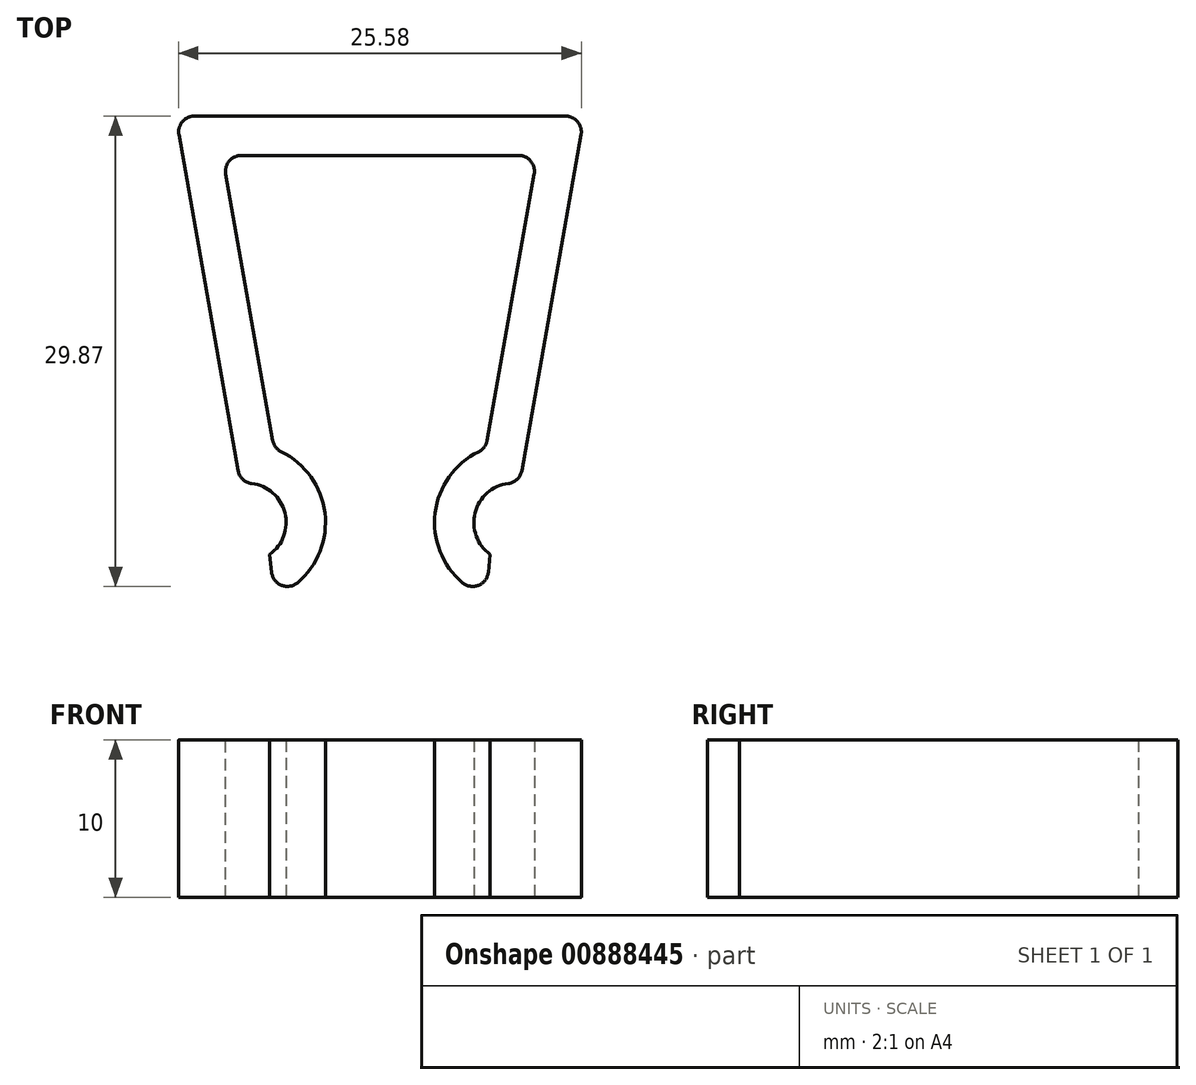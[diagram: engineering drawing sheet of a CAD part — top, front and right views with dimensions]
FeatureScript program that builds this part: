
annotation { "Feature Type Name" : "Feature", "Feature Type Description" : "" }
export const myFeature = defineFeature(function(context is Context, id is Id, definition is map)
    precondition{}
    {
        {
            var Q0;
            Q0=qCreatedBy(makeId("Top.planeOp"),FACE);
            var sketch = newSketch(context, id + "F0", { "sketchPlane" : qUnion([Q0])});
            skLineSegment(sketch, "E0", {"start": v(0, 71.12) * mm, "end": v(0, -69.02) * mm, "construction": true});
            skLineSegment(sketch, "E1", {"start": v(0, 24.9) * mm, "end": v(-10, 24.9) * mm});
            skLineSegment(sketch, "E2", {"start": v(-10, 24.9) * mm, "end": v(-6.71, 6.26) * mm});
            skArc(sketch, "E3", {"start": v(-6.71, -3.1) * mm, "mid": v(-3.46, 1.58) * mm, "end": v(-6.71, 6.26) * mm});
            skArc(sketch, "E4.0", {"start": v(-7, -0.45) * mm, "mid": v(-6.15, 2.53) * mm, "end": v(-8.86, 4.05) * mm});
            skLineSegment(sketch, "E4.1", {"start": v(-12.98, 27.4) * mm, "end": v(-8.86, 4.05) * mm});
            skLineSegment(sketch, "E4.2", {"start": v(0, 27.4) * mm, "end": v(-12.98, 27.4) * mm});
            skLineSegment(sketch, "E5", {"start": v(-7, -0.45) * mm, "end": v(-6.71, -3.1) * mm});
            skLineSegment(sketch, "E6.MirrorCS", {"start": v(0, 27.4) * mm, "end": v(12.98, 27.4) * mm});
            skLineSegment(sketch, "E7.MirrorCS", {"start": v(0, 24.9) * mm, "end": v(10, 24.9) * mm});
            skLineSegment(sketch, "E8.MirrorCS", {"start": v(12.98, 27.4) * mm, "end": v(8.86, 4.05) * mm});
            skLineSegment(sketch, "E9.MirrorCS", {"start": v(10, 24.9) * mm, "end": v(6.71, 6.26) * mm});
            skArc(sketch, "E10.MirrorCS", {"start": v(6.71, -3.1) * mm, "mid": v(3.46, 1.58) * mm, "end": v(6.71, 6.26) * mm});
            skArc(sketch, "E11.MirrorCS", {"start": v(7, -0.45) * mm, "mid": v(6.15, 2.53) * mm, "end": v(8.86, 4.05) * mm});
            skLineSegment(sketch, "E12.MirrorCS", {"start": v(7, -0.45) * mm, "end": v(6.71, -3.1) * mm});
            skSolve(sketch);
        }
        {
            var Q0;
            Q0=makeQuery(id+"F0.imprint","IMPRINT",FACE,{"disambiguationData":[TD([[makeQuery(id+"F0.imprint","IMPRINT",EDGE,{"derivedFrom":sQuery(id+"F0.wireOp",EDGE,"E1")}),-1.0]])]});
            extrude(context, id + "F1", {"entities" : qUnion([Q0]), "depth" : 10 * mm, "offsetDistance" : 25 * mm});
        }
        {
            var Q0;
            Q0=makeQuery(id+"F1.opExtrude","SWEPT_EDGE",EDGE,{"disambiguationData":[OSD([sQuery(id+"F0.wireOp",EDGE,"E3"),sQuery(id+"F0.wireOp",EDGE,"E5")])]});
            var Q1;
            Q1=makeQuery(id+"F1.opExtrude","SWEPT_EDGE",EDGE,{"disambiguationData":[OSD([sQuery(id+"F0.wireOp",EDGE,"E10.MirrorCS"),sQuery(id+"F0.wireOp",EDGE,"E12.MirrorCS")])]});
            var Q2;
            Q2=makeQuery(id+"F1.opExtrude","SWEPT_EDGE",EDGE,{"disambiguationData":[OSD([sQuery(id+"F0.wireOp",EDGE,"E4.1"),sQuery(id+"F0.wireOp",EDGE,"E4.2")])]});
            var Q3;
            Q3=makeQuery(id+"F1.opExtrude","SWEPT_EDGE",EDGE,{"disambiguationData":[OSD([sQuery(id+"F0.wireOp",EDGE,"E6.MirrorCS"),sQuery(id+"F0.wireOp",EDGE,"E8.MirrorCS")])]});
            var Q4;
            Q4=makeQuery(id+"F1.opExtrude","SWEPT_EDGE",EDGE,{"disambiguationData":[OSD([sQuery(id+"F0.wireOp",EDGE,"E1"),sQuery(id+"F0.wireOp",EDGE,"E2")])]});
            var Q5;
            Q5=makeQuery(id+"F1.opExtrude","SWEPT_EDGE",EDGE,{"disambiguationData":[OSD([sQuery(id+"F0.wireOp",EDGE,"E7.MirrorCS"),sQuery(id+"F0.wireOp",EDGE,"E9.MirrorCS")])]});
            var Q6;
            Q6=makeQuery(id+"F1.opExtrude","SWEPT_EDGE",EDGE,{"disambiguationData":[OSD([sQuery(id+"F0.wireOp",EDGE,"E2"),sQuery(id+"F0.wireOp",EDGE,"E3")])]});
            var Q7;
            Q7=makeQuery(id+"F1.opExtrude","SWEPT_EDGE",EDGE,{"disambiguationData":[OSD([sQuery(id+"F0.wireOp",EDGE,"E9.MirrorCS"),sQuery(id+"F0.wireOp",EDGE,"E10.MirrorCS")])]});
            var Q8;
            Q8=makeQuery(id+"F1.opExtrude","SWEPT_EDGE",EDGE,{"disambiguationData":[OSD([sQuery(id+"F0.wireOp",EDGE,"E4.0"),sQuery(id+"F0.wireOp",EDGE,"E4.1")])]});
            var Q9;
            Q9=makeQuery(id+"F1.opExtrude","SWEPT_EDGE",EDGE,{"disambiguationData":[OSD([sQuery(id+"F0.wireOp",EDGE,"E8.MirrorCS"),sQuery(id+"F0.wireOp",EDGE,"E11.MirrorCS")])]});
            fillet(context, id + "F2", {"entities" : qUnion([Q0, Q1, Q2, Q3, Q4, Q5, Q6, Q7, Q8, Q9]), "radius" : 1 * mm, "tangentPropagation" : true, "allowEdgeOverflow" : false});
        }
    });
